# Revit family: Furniture_Shelving-Storage_Svedholm_Millimeter
name_source: partatom
category: Furniture
revit_build: Autodesk Revit 2018 (Build: 20190510_1515(x64)
units: mm (PartAtom-declared; Revit-internal decimal feet)

## family parameters
Always vertical = No
Cut with Voids When Loaded = No
OmniClass Number = 23.21.23.00
OmniClass Title = Residential Furniture and Equipment
Room Calculation Point = No
Shared = No
Work Plane-Based = Yes

## types (2) — shared parameters
BIMobject category = Shelving & Storage
Default Elevation = 1219.2 mm  [stored 4 ft]
Description = Module-based shelf system with chrome plated wire frame and shelf in veneered oak or lacquered MDF. Bookend made of electro polished wire.
Design country = Sweden
Edition number = 1
Main material = Svedholm - Wood - Veneered Oak
Manufacturer = Svedholm
Manufacturer country = Sweden
Manufacturer name = Svedholm
Material main = Polished Chrome
Material secondary = Wood
Model = Millimeter
Product Guid = 071f43d7-fecd-4097-9304-1d16eedccc52
Product SKU = Millimeter
Product data url = https://bimobject.com
Product family = Millimeter
Product group = Storage
Product name = Millimeter
Product url = https://www.svedholm.se
QR code = https://bimobject.com
URL = https://www.svedholm.se

## per-type parameters (varying)
| type | Book end |
| ART - (412.200.004) | Yes |
| ART - (412.200.002) | No |

note: [stored X ft] marks values corroborated as IEEE doubles in the binary element streams (Revit-internal decimal feet)

## geometry (parser evidence)
native form markers: Sweep x1
no freeform markers — native parametric forms only
